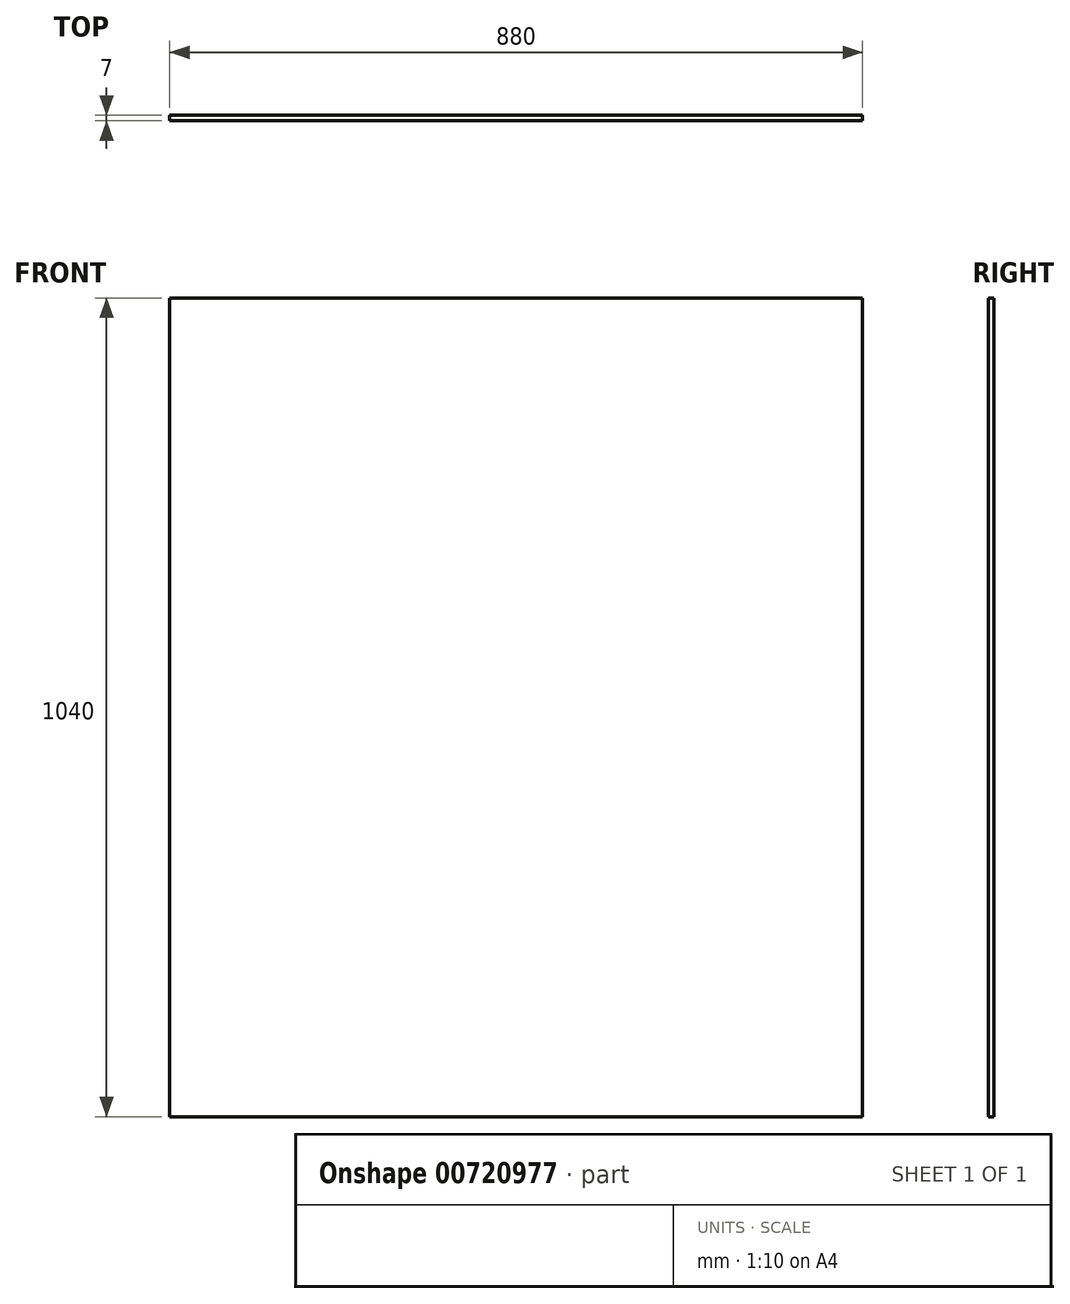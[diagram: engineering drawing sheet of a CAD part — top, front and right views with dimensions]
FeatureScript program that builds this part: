
annotation { "Feature Type Name" : "Feature", "Feature Type Description" : "" }
export const myFeature = defineFeature(function(context is Context, id is Id, definition is map)
    precondition{}
    {
        {
            var Q0;
            Q0=qCreatedBy(makeId("Front.planeOp"),FACE);
            var sketch = newSketch(context, id + "F0", { "sketchPlane" : qUnion([Q0])});
            skLineSegment(sketch, "E0.bottom", {"start": v(-375.89, 665.38) * mm, "end": v(504.11, 665.38) * mm});
            skLineSegment(sketch, "E0.top", {"start": v(-375.89, -374.62) * mm, "end": v(504.11, -374.62) * mm});
            skLineSegment(sketch, "E0.left", {"start": v(-375.89, 665.38) * mm, "end": v(-375.89, -374.62) * mm});
            skLineSegment(sketch, "E0.right", {"start": v(504.11, 665.38) * mm, "end": v(504.11, -374.62) * mm});
            skSolve(sketch);
        }
        {
            var Q0;
            Q0=makeQuery(id+"F0.imprint","IMPRINT",FACE,{"disambiguationData":[TD([[makeQuery(id+"F0.imprint","IMPRINT",EDGE,{"derivedFrom":sQuery(id+"F0.wireOp",EDGE,"E0.bottom")}),-1.0]])]});
            cPlane(context, id + "F1", {"entities" : qUnion([Q0]), "cplaneType" : CPlaneType.OFFSET, "offset" : 25 * mm, "width" : 150 * mm, "height" : 150 * mm});
        }
        {
            var Q0;
            Q0=makeQuery(id+"F0.imprint","IMPRINT",FACE,{"disambiguationData":[TD([[makeQuery(id+"F0.imprint","IMPRINT",EDGE,{"derivedFrom":sQuery(id+"F0.wireOp",EDGE,"E0.bottom")}),-1.0]])]});
            extrude(context, id + "F2", {"entities" : qUnion([Q0]), "depth" : 7 * mm, "offsetDistance" : 25 * mm});
        }
    });
